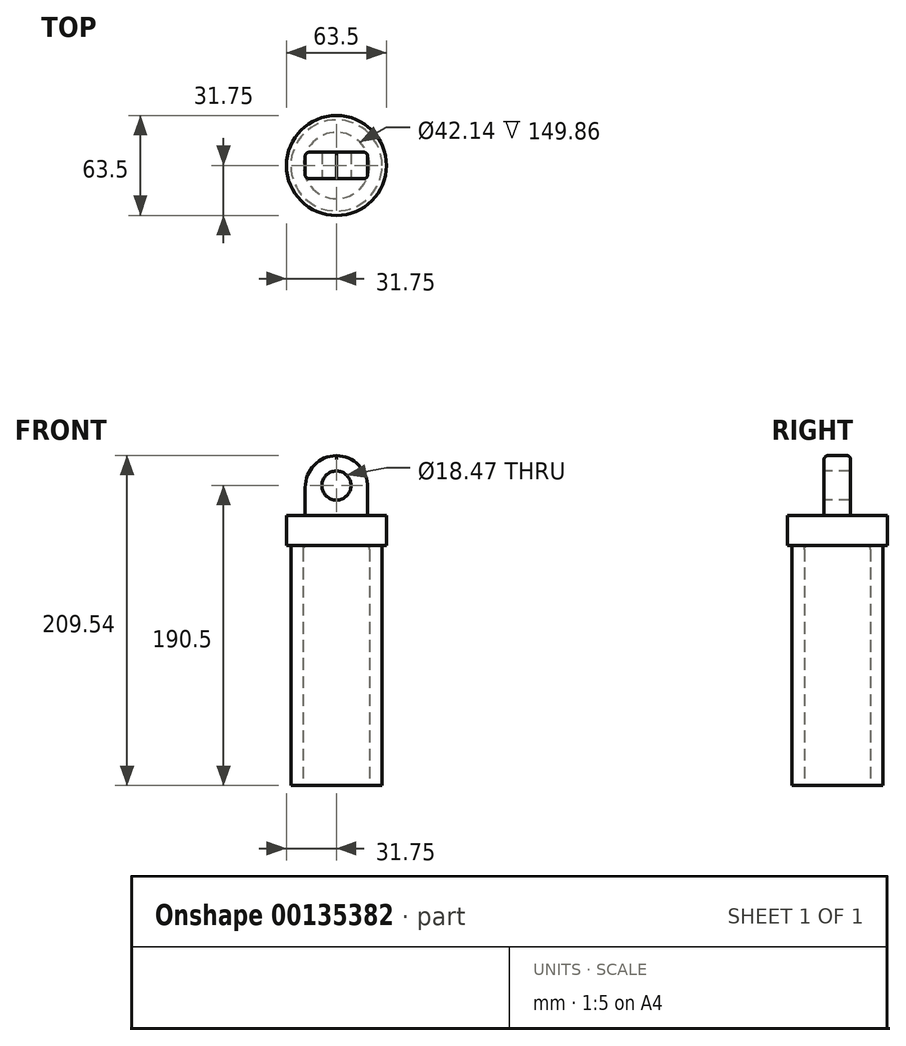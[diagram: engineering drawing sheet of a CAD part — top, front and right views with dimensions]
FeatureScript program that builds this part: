
annotation { "Feature Type Name" : "Feature", "Feature Type Description" : "" }
export const myFeature = defineFeature(function(context is Context, id is Id, definition is map)
    precondition{}
    {
        {
            var Q0;
            Q0=qCreatedBy(makeId("Top.planeOp"),FACE);
            var sketch = newSketch(context, id + "F0", { "sketchPlane" : qUnion([Q0])});
            skCircle(sketch, "E0", {"center": v(0, 0) * mm, "radius": 28.95 * mm});
            skCircle(sketch, "E1", {"center": v(0, 0) * mm, "radius": 21.07 * mm});
            skSolve(sketch);
        }
        {
            var Q0;
            Q0 = qSketchRegion(id + "F0", true);
            extrude(context, id + "F1", {"entities" : qUnion([Q0]), "depth" : 152.4 * mm});
        }
        {
            var Q0;
            Q0=makeQuery(id+"F1.opExtrude","CAP_FACE",FACE,{"disambiguationData":[OSD([sQuery(id+"F0.wireOp",EDGE,"E0"),sQuery(id+"F0.wireOp",EDGE,"E1")])],"isStart":false});
            var sketch = newSketch(context, id + "F2", { "sketchPlane" : qUnion([Q0])});
            skCircle(sketch, "E2", {"center": v(0, 0) * mm, "radius": 31.75 * mm});
            skSolve(sketch);
        }
        {
            var Q0;
            Q0 = qSketchRegion(id + "F2", true);
            extrude(context, id + "F3", {"entities" : qUnion([Q0]), "operationType" : NewBodyOperationType.ADD, "depth" : 19.05 * mm});
        }
        {
            var Q0;
            Q0=makeQuery(id+"F3.opExtrude","CAP_FACE",FACE,{"disambiguationData":[OSD([sQuery(id+"F2.wireOp",EDGE,"E2")])],"isStart":false});
            var sketch = newSketch(context, id + "F4", { "sketchPlane" : qUnion([Q0])});
            skLineSegment(sketch, "E3.bottom", {"start": v(19.86, -8.42) * mm, "end": v(-19.86, -8.42) * mm});
            skLineSegment(sketch, "E3.top", {"start": v(19.86, 8.42) * mm, "end": v(-19.86, 8.42) * mm});
            skLineSegment(sketch, "E3.left", {"start": v(19.86, -8.42) * mm, "end": v(19.86, 8.42) * mm});
            skLineSegment(sketch, "E3.right", {"start": v(-19.86, -8.42) * mm, "end": v(-19.86, 8.42) * mm});
            skPoint(sketch, "E3.middle", {"position": v(0, 0) * mm});
            skSolve(sketch);
        }
        {
            var Q0;
            Q0 = qSketchRegion(id + "F4", true);
            extrude(context, id + "F5", {"entities" : qUnion([Q0]), "operationType" : NewBodyOperationType.ADD, "depth" : 38.1 * mm});
        }
        {
            var Q0;
            Q0=makeQuery(id+"F5.opExtrude","SWEPT_FACE",FACE,{"disambiguationData":[OSD([sQuery(id+"F4.wireOp",EDGE,"E3.bottom")])]});
            var sketch = newSketch(context, id + "F6", { "sketchPlane" : qUnion([Q0])});
            skCircle(sketch, "E4", {"center": v(0, 190.5) * mm, "radius": 9.23 * mm});
            skPoint(sketch, "E4.centerSnap0", {"position": v(-19.86, 190.5) * mm});
            skSolve(sketch);
        }
        {
            var Q0;
            Q0 = qSketchRegion(id + "F6", true);
            extrude(context, id + "F7", {"entities" : qUnion([Q0]), "operationType" : NewBodyOperationType.REMOVE, "oppositeDirection" : true, "depth" : 25.4 * mm});
        }
        {
            var Q0;
            Q0=makeQuery(id+"F5.opExtrude","CAP_EDGE",EDGE,{"disambiguationData":[OSD([sQuery(id+"F4.wireOp",EDGE,"E3.left")])],"isStart":false});
            var Q1;
            Q1=makeQuery(id+"F5.opExtrude","CAP_EDGE",EDGE,{"disambiguationData":[OSD([sQuery(id+"F4.wireOp",EDGE,"E3.right")])],"isStart":false});
            fillet(context, id + "F8", {"entities" : qUnion([Q0, Q1]), "radius" : 20.32 * mm, "tangentPropagation" : true, "allowEdgeOverflow" : false});
        }
        {
            var Q0;
            Q0=makeQuery(id+"F5.opExtrude","SWEPT_EDGE",EDGE,{"disambiguationData":[OSD([sQuery(id+"F4.wireOp",EDGE,"E3.bottom"),sQuery(id+"F4.wireOp",EDGE,"E3.left")])]});
            var Q1;
            Q1=makeQuery(id+"F8.opFillet","BLEND_EDGE",EDGE,{"blendedFrom":[makeQuery(id+"F5.opExtrude","CAP_EDGE",EDGE,{"disambiguationData":[OSD([sQuery(id+"F4.wireOp",EDGE,"E3.left")])],"isStart":false}),makeQuery(id+"F5.opExtrude","SWEPT_FACE",FACE,{"disambiguationData":[OSD([sQuery(id+"F4.wireOp",EDGE,"E3.bottom")])]})],"blendedInto":[makeQuery(id+"F5.opExtrude","SWEPT_FACE",FACE,{"disambiguationData":[OSD([sQuery(id+"F4.wireOp",EDGE,"E3.bottom")])]})]});
            var Q2;
            Q2=makeQuery(id+"F8.opFillet","BLEND_EDGE",EDGE,{"blendedFrom":[makeQuery(id+"F5.opExtrude","CAP_EDGE",EDGE,{"disambiguationData":[OSD([sQuery(id+"F4.wireOp",EDGE,"E3.right")])],"isStart":false}),makeQuery(id+"F5.opExtrude","SWEPT_FACE",FACE,{"disambiguationData":[OSD([sQuery(id+"F4.wireOp",EDGE,"E3.bottom")])]})],"blendedInto":[makeQuery(id+"F5.opExtrude","SWEPT_FACE",FACE,{"disambiguationData":[OSD([sQuery(id+"F4.wireOp",EDGE,"E3.bottom")])]})]});
            var Q3;
            Q3=makeQuery(id+"F5.opExtrude","SWEPT_EDGE",EDGE,{"disambiguationData":[OSD([sQuery(id+"F4.wireOp",EDGE,"E3.bottom"),sQuery(id+"F4.wireOp",EDGE,"E3.right")])]});
            var Q4;
            Q4=makeQuery(id+"F5.opExtrude","CAP_EDGE",EDGE,{"disambiguationData":[OSD([sQuery(id+"F4.wireOp",EDGE,"E3.bottom")])],"isStart":true});
            var Q5;
            Q5=makeQuery(id+"F5.opExtrude","CAP_EDGE",EDGE,{"disambiguationData":[OSD([sQuery(id+"F4.wireOp",EDGE,"E3.left")])],"isStart":true});
            var Q6;
            Q6=makeQuery(id+"F1.opExtrude","CAP_EDGE",EDGE,{"disambiguationData":[OSD([sQuery(id+"F0.wireOp",EDGE,"E0")])],"isStart":false});
            var Q7;
            Q7=makeQuery(id+"F1.opExtrude","CAP_EDGE",EDGE,{"disambiguationData":[OSD([sQuery(id+"F0.wireOp",EDGE,"E1")])],"isStart":false});
            var Q8;
            Q8=makeQuery(id+"F5.opExtrude","SWEPT_EDGE",EDGE,{"disambiguationData":[OSD([sQuery(id+"F4.wireOp",EDGE,"E3.top"),sQuery(id+"F4.wireOp",EDGE,"E3.left")])]});
            var Q9;
            Q9=makeQuery(id+"F8.opFillet","BLEND_EDGE",EDGE,{"blendedFrom":[makeQuery(id+"F5.opExtrude","CAP_EDGE",EDGE,{"disambiguationData":[OSD([sQuery(id+"F4.wireOp",EDGE,"E3.left")])],"isStart":false}),makeQuery(id+"F5.opExtrude","SWEPT_FACE",FACE,{"disambiguationData":[OSD([sQuery(id+"F4.wireOp",EDGE,"E3.top")])]})],"blendedInto":[makeQuery(id+"F5.opExtrude","SWEPT_FACE",FACE,{"disambiguationData":[OSD([sQuery(id+"F4.wireOp",EDGE,"E3.top")])]})]});
            var Q10;
            Q10=makeQuery(id+"F8.opFillet","BLEND_EDGE",EDGE,{"blendedFrom":[makeQuery(id+"F5.opExtrude","CAP_EDGE",EDGE,{"disambiguationData":[OSD([sQuery(id+"F4.wireOp",EDGE,"E3.right")])],"isStart":false}),makeQuery(id+"F5.opExtrude","SWEPT_FACE",FACE,{"disambiguationData":[OSD([sQuery(id+"F4.wireOp",EDGE,"E3.top")])]})],"blendedInto":[makeQuery(id+"F5.opExtrude","SWEPT_FACE",FACE,{"disambiguationData":[OSD([sQuery(id+"F4.wireOp",EDGE,"E3.top")])]})]});
            fillet(context, id + "F9", {"entities" : qUnion([Q0, Q1, Q2, Q3, Q4, Q5, Q6, Q7, Q8, Q9, Q10]), "radius" : 2.54 * mm, "tangentPropagation" : true, "allowEdgeOverflow" : false});
        }
    });
